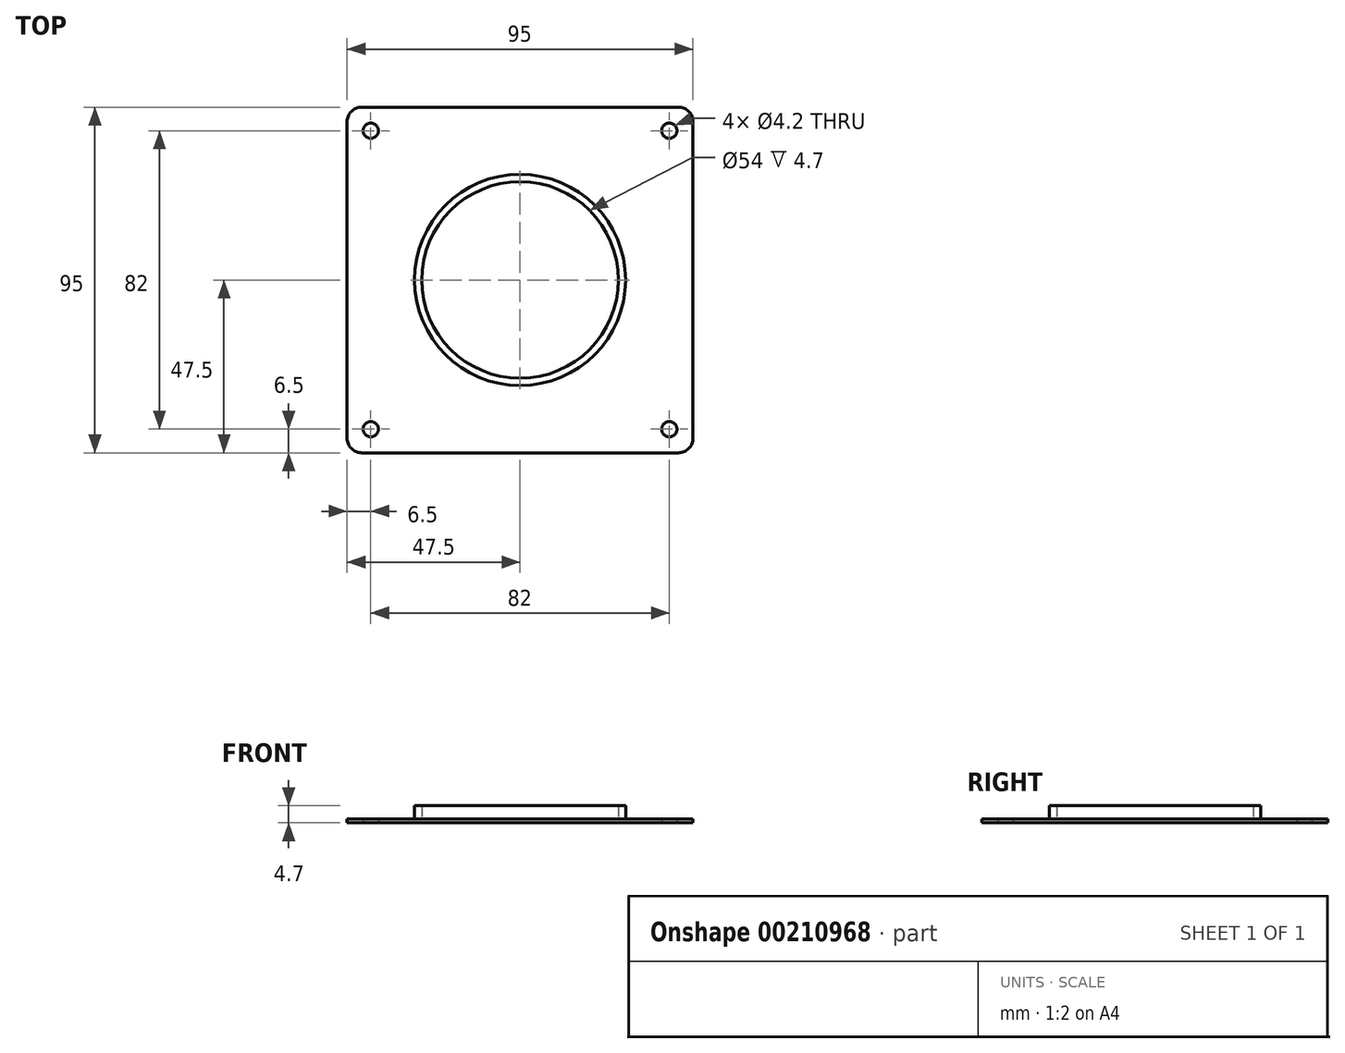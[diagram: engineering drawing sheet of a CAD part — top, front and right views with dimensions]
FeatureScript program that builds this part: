
annotation { "Feature Type Name" : "Feature", "Feature Type Description" : "" }
export const myFeature = defineFeature(function(context is Context, id is Id, definition is map)
    precondition{}
    {
        {
            var Q0;
            Q0=qCreatedBy(makeId("Top.planeOp"),FACE);
            var sketch = newSketch(context, id + "F0", { "sketchPlane" : qUnion([Q0])});
            skLineSegment(sketch, "E0.bottom", {"start": v(43.5, -47.5) * mm, "end": v(-43.5, -47.5) * mm});
            skLineSegment(sketch, "E0.top", {"start": v(43.5, 47.5) * mm, "end": v(-43.5, 47.5) * mm});
            skLineSegment(sketch, "E0.left", {"start": v(47.5, -43.5) * mm, "end": v(47.5, 43.5) * mm});
            skLineSegment(sketch, "E0.right", {"start": v(-47.5, -43.5) * mm, "end": v(-47.5, 43.5) * mm});
            skPoint(sketch, "E0.middle", {"position": v(0, 0) * mm});
            skCircle(sketch, "E1", {"center": v(0, 0) * mm, "radius": 27 * mm});
            skCircle(sketch, "E2.0", {"center": v(0, 0) * mm, "radius": 29 * mm});
            skCircle(sketch, "E3", {"center": v(-41, 41) * mm, "radius": 2.1 * mm});
            skCircle(sketch, "E4.MirrorC", {"center": v(41, 41) * mm, "radius": 2.1 * mm});
            skCircle(sketch, "E5.MirrorC", {"center": v(41, -41) * mm, "radius": 2.1 * mm});
            skCircle(sketch, "E6.MirrorC", {"center": v(-41, -41) * mm, "radius": 2.1 * mm});
            skPoint(sketch, "E7.visualSharp", {"position": v(-47.5, 47.5) * mm});
            skArc(sketch, "E7.filletArc", {"start": v(-43.5, 47.5) * mm, "mid": v(-46.33, 46.33) * mm, "end": v(-47.5, 43.5) * mm});
            skPoint(sketch, "E8.visualSharp", {"position": v(47.5, 47.5) * mm});
            skArc(sketch, "E8.filletArc", {"start": v(47.5, 43.5) * mm, "mid": v(46.33, 46.33) * mm, "end": v(43.5, 47.5) * mm});
            skPoint(sketch, "E9.visualSharp", {"position": v(47.5, -47.5) * mm});
            skArc(sketch, "E9.filletArc", {"start": v(43.5, -47.5) * mm, "mid": v(46.33, -46.33) * mm, "end": v(47.5, -43.5) * mm});
            skPoint(sketch, "E10.visualSharp", {"position": v(-47.5, -47.5) * mm});
            skArc(sketch, "E10.filletArc", {"start": v(-47.5, -43.5) * mm, "mid": v(-46.33, -46.33) * mm, "end": v(-43.5, -47.5) * mm});
            skSolve(sketch);
        }
        {
            var Q0;
            Q0=makeQuery(id+"F0.imprint","IMPRINT",FACE,{"disambiguationData":[TD([[makeQuery(id+"F0.imprint","IMPRINT",EDGE,{"derivedFrom":sQuery(id+"F0.wireOp",EDGE,"E0.bottom")}),-1.0]])]});
            var Q1;
            Q1=makeQuery(id+"F0.imprint","IMPRINT",FACE,{"disambiguationData":[TD([[makeQuery(id+"F0.imprint","IMPRINT",EDGE,{"derivedFrom":sQuery(id+"F0.wireOp",EDGE,"E1")}),-1.0]])]});
            extrude(context, id + "F1", {"entities" : qUnion([Q0, Q1]), "depth" : 1 * mm});
        }
        {
            var Q0;
            Q0=makeQuery(id+"F0.imprint","IMPRINT",FACE,{"disambiguationData":[TD([[makeQuery(id+"F0.imprint","IMPRINT",EDGE,{"derivedFrom":sQuery(id+"F0.wireOp",EDGE,"E1")}),-1.0]])]});
            extrude(context, id + "F2", {"entities" : qUnion([Q0]), "operationType" : NewBodyOperationType.ADD, "depth" : 4.7 * mm});
        }
    });
